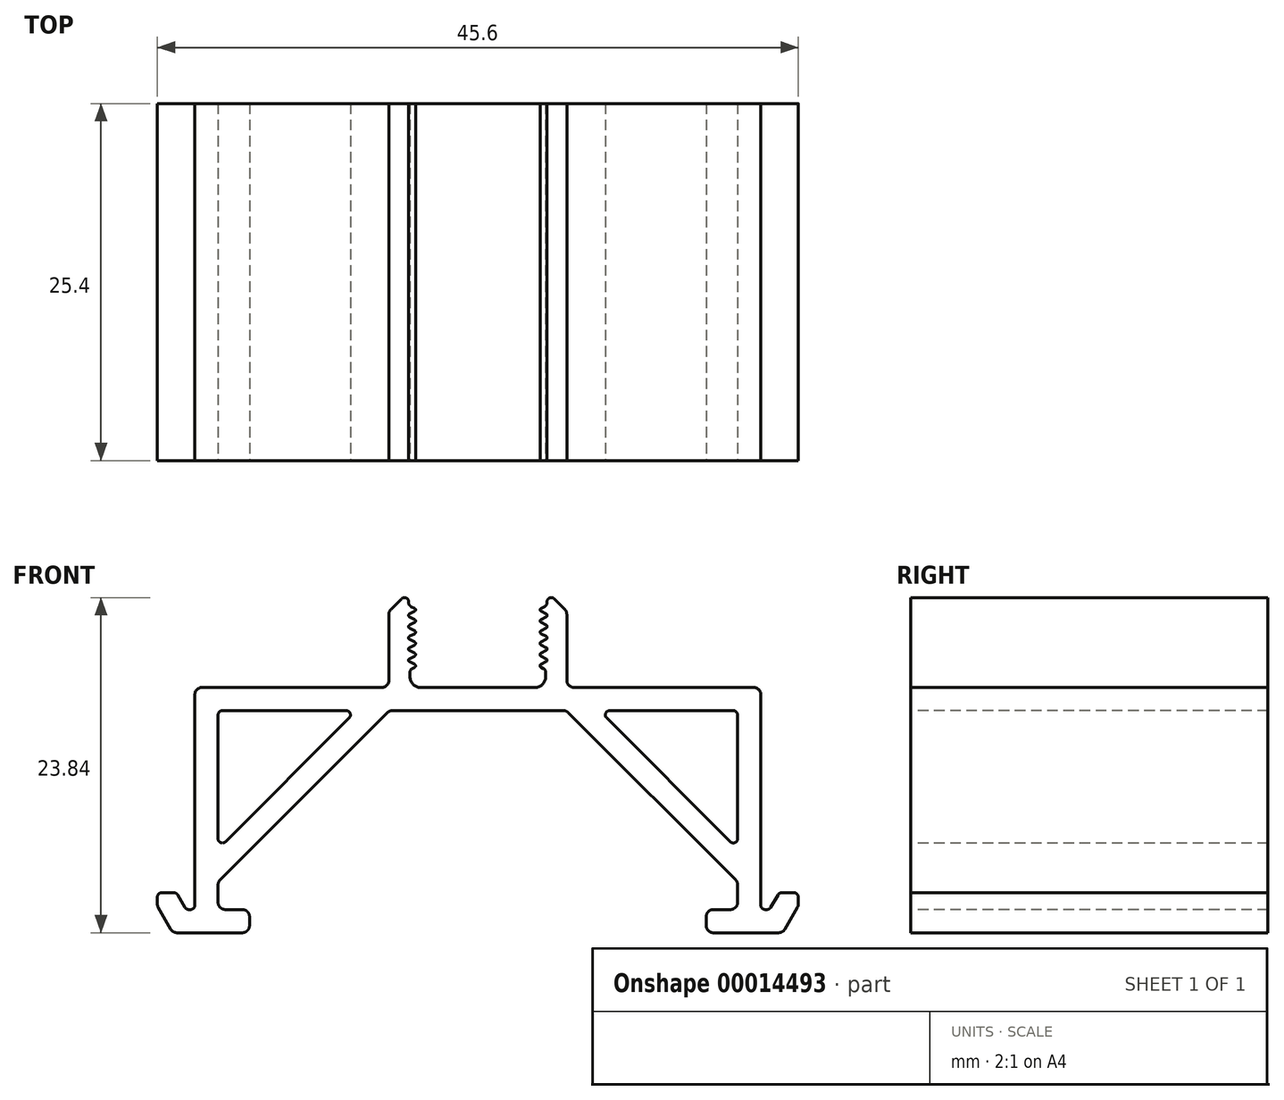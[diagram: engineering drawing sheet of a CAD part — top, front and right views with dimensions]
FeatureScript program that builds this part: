
annotation { "Feature Type Name" : "Feature", "Feature Type Description" : "" }
export const myFeature = defineFeature(function(context is Context, id is Id, definition is map)
    precondition{}
    {
        {
            var Q0;
            Q0=qCreatedBy(makeId("Front.planeOp"),FACE);
            var sketch = newSketch(context, id + "F0", { "sketchPlane" : qUnion([Q0])});
            skArc(sketch, "E0", {"start": v(18.48, 3.57) * mm, "mid": v(18.39, 3.79) * mm, "end": v(18.17, 3.88) * mm});
            skLineSegment(sketch, "E1", {"start": v(9.37, 3.88) * mm, "end": v(18.17, 3.88) * mm});
            skArc(sketch, "E2", {"start": v(9.37, 3.88) * mm, "mid": v(9.09, 3.69) * mm, "end": v(9.15, 3.36) * mm});
            skLineSegment(sketch, "E3", {"start": v(17.96, -5.45) * mm, "end": v(9.15, 3.36) * mm});
            skArc(sketch, "E4", {"start": v(17.96, -5.45) * mm, "mid": v(18.3, -5.51) * mm, "end": v(18.48, -5.23) * mm});
            skLineSegment(sketch, "E5", {"start": v(18.48, 3.57) * mm, "end": v(18.48, -5.23) * mm});
            skLineSegment(sketch, "E6", {"start": v(-18.48, -5.23) * mm, "end": v(-18.48, 3.57) * mm});
            skArc(sketch, "E7", {"start": v(-18.48, -5.23) * mm, "mid": v(-18.3, -5.51) * mm, "end": v(-17.96, -5.45) * mm});
            skLineSegment(sketch, "E8", {"start": v(-9.15, 3.36) * mm, "end": v(-17.96, -5.45) * mm});
            skArc(sketch, "E9", {"start": v(-9.15, 3.36) * mm, "mid": v(-9.09, 3.69) * mm, "end": v(-9.37, 3.88) * mm});
            skLineSegment(sketch, "E10", {"start": v(-18.17, 3.88) * mm, "end": v(-9.37, 3.88) * mm});
            skArc(sketch, "E11", {"start": v(-18.17, 3.88) * mm, "mid": v(-18.39, 3.79) * mm, "end": v(-18.48, 3.57) * mm});
            skLineSegment(sketch, "E12", {"start": v(4.86, 10.55) * mm, "end": v(4.5, 10.36) * mm});
            skArc(sketch, "E13", {"start": v(4.5, 10.36) * mm, "mid": v(4.43, 10.26) * mm, "end": v(4.5, 10.15) * mm});
            skLineSegment(sketch, "E14", {"start": v(4.5, 10.15) * mm, "end": v(4.86, 9.97) * mm});
            skArc(sketch, "E15", {"start": v(4.86, 9.75) * mm, "mid": v(4.93, 9.86) * mm, "end": v(4.86, 9.97) * mm});
            skLineSegment(sketch, "E16", {"start": v(4.86, 9.75) * mm, "end": v(4.5, 9.57) * mm});
            skArc(sketch, "E17", {"start": v(4.5, 9.57) * mm, "mid": v(4.43, 9.46) * mm, "end": v(4.5, 9.35) * mm});
            skLineSegment(sketch, "E18", {"start": v(4.5, 9.35) * mm, "end": v(4.86, 9.17) * mm});
            skArc(sketch, "E19", {"start": v(4.86, 8.95) * mm, "mid": v(4.93, 9.06) * mm, "end": v(4.86, 9.17) * mm});
            skLineSegment(sketch, "E20", {"start": v(4.86, 8.95) * mm, "end": v(4.5, 8.77) * mm});
            skArc(sketch, "E21", {"start": v(4.5, 8.77) * mm, "mid": v(4.43, 8.66) * mm, "end": v(4.5, 8.56) * mm});
            skLineSegment(sketch, "E22", {"start": v(4.5, 8.56) * mm, "end": v(4.86, 8.37) * mm});
            skArc(sketch, "E23", {"start": v(4.86, 8.16) * mm, "mid": v(4.93, 8.26) * mm, "end": v(4.86, 8.37) * mm});
            skLineSegment(sketch, "E24", {"start": v(4.86, 8.16) * mm, "end": v(4.5, 7.97) * mm});
            skArc(sketch, "E25", {"start": v(4.5, 7.97) * mm, "mid": v(4.43, 7.86) * mm, "end": v(4.5, 7.76) * mm});
            skLineSegment(sketch, "E26", {"start": v(4.5, 7.76) * mm, "end": v(4.86, 7.57) * mm});
            skArc(sketch, "E27", {"start": v(4.86, 7.36) * mm, "mid": v(4.93, 7.47) * mm, "end": v(4.86, 7.57) * mm});
            skLineSegment(sketch, "E28", {"start": v(4.86, 7.36) * mm, "end": v(4.5, 7.17) * mm});
            skArc(sketch, "E29", {"start": v(4.5, 7.17) * mm, "mid": v(4.43, 7.07) * mm, "end": v(4.5, 6.96) * mm});
            skLineSegment(sketch, "E30", {"start": v(4.5, 6.96) * mm, "end": v(4.66, 6.88) * mm});
            skArc(sketch, "E31", {"start": v(4.83, 6.6) * mm, "mid": v(4.78, 6.77) * mm, "end": v(4.66, 6.88) * mm});
            skLineSegment(sketch, "E32", {"start": v(4.83, 6.6) * mm, "end": v(4.83, 6.3) * mm});
            skArc(sketch, "E33", {"start": v(4.07, 5.53) * mm, "mid": v(4.6, 5.75) * mm, "end": v(4.83, 6.3) * mm});
            skLineSegment(sketch, "E34", {"start": v(4.07, 5.53) * mm, "end": v(-4.07, 5.53) * mm});
            skArc(sketch, "E35", {"start": v(-4.83, 6.3) * mm, "mid": v(-4.6, 5.75) * mm, "end": v(-4.07, 5.53) * mm});
            skLineSegment(sketch, "E36", {"start": v(-4.83, 6.3) * mm, "end": v(-4.83, 6.6) * mm});
            skArc(sketch, "E37", {"start": v(-4.66, 6.88) * mm, "mid": v(-4.78, 6.77) * mm, "end": v(-4.83, 6.6) * mm});
            skLineSegment(sketch, "E38", {"start": v(-4.66, 6.88) * mm, "end": v(-4.5, 6.96) * mm});
            skArc(sketch, "E39", {"start": v(-4.5, 6.96) * mm, "mid": v(-4.43, 7.07) * mm, "end": v(-4.5, 7.17) * mm});
            skLineSegment(sketch, "E40", {"start": v(-4.5, 7.17) * mm, "end": v(-4.86, 7.36) * mm});
            skArc(sketch, "E41", {"start": v(-4.86, 7.57) * mm, "mid": v(-4.93, 7.47) * mm, "end": v(-4.86, 7.36) * mm});
            skLineSegment(sketch, "E42", {"start": v(-4.86, 7.57) * mm, "end": v(-4.5, 7.76) * mm});
            skArc(sketch, "E43", {"start": v(-4.5, 7.76) * mm, "mid": v(-4.43, 7.86) * mm, "end": v(-4.5, 7.97) * mm});
            skLineSegment(sketch, "E44", {"start": v(-4.5, 7.97) * mm, "end": v(-4.86, 8.16) * mm});
            skArc(sketch, "E45", {"start": v(-4.86, 8.37) * mm, "mid": v(-4.93, 8.26) * mm, "end": v(-4.86, 8.16) * mm});
            skLineSegment(sketch, "E46", {"start": v(-4.86, 8.37) * mm, "end": v(-4.5, 8.56) * mm});
            skArc(sketch, "E47", {"start": v(-4.5, 8.56) * mm, "mid": v(-4.43, 8.66) * mm, "end": v(-4.5, 8.77) * mm});
            skLineSegment(sketch, "E48", {"start": v(-4.5, 8.77) * mm, "end": v(-4.86, 8.95) * mm});
            skArc(sketch, "E49", {"start": v(-4.86, 9.17) * mm, "mid": v(-4.93, 9.06) * mm, "end": v(-4.86, 8.95) * mm});
            skLineSegment(sketch, "E50", {"start": v(-4.86, 9.17) * mm, "end": v(-4.5, 9.35) * mm});
            skArc(sketch, "E51", {"start": v(-4.5, 9.35) * mm, "mid": v(-4.43, 9.46) * mm, "end": v(-4.5, 9.57) * mm});
            skLineSegment(sketch, "E52", {"start": v(-4.5, 9.57) * mm, "end": v(-4.86, 9.75) * mm});
            skArc(sketch, "E53", {"start": v(-4.86, 9.97) * mm, "mid": v(-4.93, 9.86) * mm, "end": v(-4.86, 9.75) * mm});
            skLineSegment(sketch, "E54", {"start": v(-4.86, 9.97) * mm, "end": v(-4.5, 10.15) * mm});
            skArc(sketch, "E55", {"start": v(-4.5, 10.15) * mm, "mid": v(-4.43, 10.26) * mm, "end": v(-4.5, 10.36) * mm});
            skLineSegment(sketch, "E56", {"start": v(-4.5, 10.36) * mm, "end": v(-4.86, 10.55) * mm});
            skArc(sketch, "E57", {"start": v(-4.86, 10.76) * mm, "mid": v(-4.93, 10.66) * mm, "end": v(-4.86, 10.55) * mm});
            skLineSegment(sketch, "E58", {"start": v(-4.86, 10.76) * mm, "end": v(-4.5, 10.95) * mm});
            skArc(sketch, "E59", {"start": v(-4.5, 10.95) * mm, "mid": v(-4.43, 11.06) * mm, "end": v(-4.5, 11.16) * mm});
            skLineSegment(sketch, "E60", {"start": v(-4.5, 11.16) * mm, "end": v(-4.76, 11.3) * mm});
            skArc(sketch, "E61", {"start": v(-4.92, 11.6) * mm, "mid": v(-4.88, 11.42) * mm, "end": v(-4.76, 11.3) * mm});
            skArc(sketch, "E62", {"start": v(-4.92, 11.6) * mm, "mid": v(-5.1, 11.9) * mm, "end": v(-5.44, 11.83) * mm});
            skLineSegment(sketch, "E63", {"start": v(-5.44, 11.83) * mm, "end": v(-6.18, 11.1) * mm});
            skArc(sketch, "E64", {"start": v(-6.18, 11.1) * mm, "mid": v(-6.29, 10.93) * mm, "end": v(-6.33, 10.74) * mm});
            skLineSegment(sketch, "E65", {"start": v(-6.33, 10.74) * mm, "end": v(-6.33, 6.04) * mm});
            skArc(sketch, "E66", {"start": v(-6.83, 5.53) * mm, "mid": v(-6.48, 5.68) * mm, "end": v(-6.33, 6.04) * mm});
            skLineSegment(sketch, "E67", {"start": v(-6.83, 5.53) * mm, "end": v(-19.62, 5.53) * mm});
            skArc(sketch, "E68", {"start": v(-19.62, 5.53) * mm, "mid": v(-19.98, 5.38) * mm, "end": v(-20.13, 5.02) * mm});
            skLineSegment(sketch, "E69", {"start": v(-20.13, 5.02) * mm, "end": v(-20.13, -9.96) * mm});
            skArc(sketch, "E70", {"start": v(-20.43, -10.27) * mm, "mid": v(-20.22, -10.18) * mm, "end": v(-20.13, -9.96) * mm});
            skLineSegment(sketch, "E71", {"start": v(-20.43, -10.27) * mm, "end": v(-20.57, -10.27) * mm});
            skArc(sketch, "E72", {"start": v(-20.83, -10.12) * mm, "mid": v(-20.72, -10.23) * mm, "end": v(-20.57, -10.27) * mm});
            skLineSegment(sketch, "E73", {"start": v(-20.83, -10.12) * mm, "end": v(-21.34, -9.23) * mm});
            skArc(sketch, "E74", {"start": v(-21.34, -9.23) * mm, "mid": v(-21.46, -9.12) * mm, "end": v(-21.6, -9.08) * mm});
            skLineSegment(sketch, "E75", {"start": v(-21.6, -9.08) * mm, "end": v(-22.5, -9.08) * mm});
            skArc(sketch, "E76", {"start": v(-22.5, -9.08) * mm, "mid": v(-22.7, -9.17) * mm, "end": v(-22.8, -9.38) * mm});
            skLineSegment(sketch, "E77", {"start": v(-22.8, -9.38) * mm, "end": v(-22.8, -9.88) * mm});
            skArc(sketch, "E78", {"start": v(-22.8, -9.88) * mm, "mid": v(-22.78, -10.01) * mm, "end": v(-22.73, -10.13) * mm});
            skLineSegment(sketch, "E79", {"start": v(-22.73, -10.13) * mm, "end": v(-21.84, -11.67) * mm});
            skArc(sketch, "E80", {"start": v(-21.84, -11.67) * mm, "mid": v(-21.66, -11.85) * mm, "end": v(-21.4, -11.92) * mm});
            skLineSegment(sketch, "E81", {"start": v(-21.4, -11.92) * mm, "end": v(-16.75, -11.92) * mm});
            skArc(sketch, "E82", {"start": v(-16.75, -11.92) * mm, "mid": v(-16.4, -11.77) * mm, "end": v(-16.24, -11.41) * mm});
            skLineSegment(sketch, "E83", {"start": v(-16.24, -11.41) * mm, "end": v(-16.24, -10.78) * mm});
            skArc(sketch, "E84", {"start": v(-16.24, -10.78) * mm, "mid": v(-16.4, -10.42) * mm, "end": v(-16.75, -10.27) * mm});
            skLineSegment(sketch, "E85", {"start": v(-16.75, -10.27) * mm, "end": v(-17.97, -10.27) * mm});
            skArc(sketch, "E86", {"start": v(-18.48, -9.76) * mm, "mid": v(-18.33, -10.12) * mm, "end": v(-17.97, -10.27) * mm});
            skLineSegment(sketch, "E87", {"start": v(-18.48, -9.76) * mm, "end": v(-18.48, -8.51) * mm});
            skArc(sketch, "E88", {"start": v(-18.33, -8.15) * mm, "mid": v(-18.44, -8.32) * mm, "end": v(-18.48, -8.51) * mm});
            skLineSegment(sketch, "E89", {"start": v(-18.33, -8.15) * mm, "end": v(-6.45, 3.73) * mm});
            skArc(sketch, "E90", {"start": v(-6.09, 3.88) * mm, "mid": v(-6.28, 3.84) * mm, "end": v(-6.45, 3.73) * mm});
            skLineSegment(sketch, "E91", {"start": v(-6.09, 3.88) * mm, "end": v(6.09, 3.88) * mm});
            skArc(sketch, "E92", {"start": v(6.45, 3.73) * mm, "mid": v(6.28, 3.84) * mm, "end": v(6.09, 3.88) * mm});
            skLineSegment(sketch, "E93", {"start": v(6.45, 3.73) * mm, "end": v(18.33, -8.15) * mm});
            skArc(sketch, "E94", {"start": v(18.48, -8.51) * mm, "mid": v(18.44, -8.32) * mm, "end": v(18.33, -8.15) * mm});
            skLineSegment(sketch, "E95", {"start": v(18.48, -8.51) * mm, "end": v(18.48, -9.76) * mm});
            skArc(sketch, "E96", {"start": v(17.97, -10.27) * mm, "mid": v(18.33, -10.12) * mm, "end": v(18.48, -9.76) * mm});
            skLineSegment(sketch, "E97", {"start": v(17.97, -10.27) * mm, "end": v(16.75, -10.27) * mm});
            skArc(sketch, "E98", {"start": v(16.75, -10.27) * mm, "mid": v(16.4, -10.42) * mm, "end": v(16.24, -10.78) * mm});
            skLineSegment(sketch, "E99", {"start": v(16.24, -10.78) * mm, "end": v(16.24, -11.41) * mm});
            skArc(sketch, "E100", {"start": v(16.24, -11.41) * mm, "mid": v(16.4, -11.77) * mm, "end": v(16.75, -11.92) * mm});
            skLineSegment(sketch, "E101", {"start": v(16.75, -11.92) * mm, "end": v(21.4, -11.92) * mm});
            skArc(sketch, "E102", {"start": v(21.4, -11.92) * mm, "mid": v(21.66, -11.85) * mm, "end": v(21.84, -11.67) * mm});
            skLineSegment(sketch, "E103", {"start": v(21.84, -11.67) * mm, "end": v(22.73, -10.13) * mm});
            skArc(sketch, "E104", {"start": v(22.73, -10.13) * mm, "mid": v(22.78, -10.01) * mm, "end": v(22.8, -9.88) * mm});
            skLineSegment(sketch, "E105", {"start": v(22.8, -9.88) * mm, "end": v(22.8, -9.38) * mm});
            skArc(sketch, "E106", {"start": v(22.8, -9.38) * mm, "mid": v(22.7, -9.17) * mm, "end": v(22.5, -9.08) * mm});
            skLineSegment(sketch, "E107", {"start": v(22.5, -9.08) * mm, "end": v(21.6, -9.08) * mm});
            skArc(sketch, "E108", {"start": v(21.6, -9.08) * mm, "mid": v(21.46, -9.12) * mm, "end": v(21.34, -9.23) * mm});
            skLineSegment(sketch, "E109", {"start": v(21.34, -9.23) * mm, "end": v(20.83, -10.12) * mm});
            skArc(sketch, "E110", {"start": v(20.57, -10.27) * mm, "mid": v(20.72, -10.23) * mm, "end": v(20.83, -10.12) * mm});
            skLineSegment(sketch, "E111", {"start": v(20.57, -10.27) * mm, "end": v(20.43, -10.27) * mm});
            skArc(sketch, "E112", {"start": v(20.13, -9.96) * mm, "mid": v(20.22, -10.18) * mm, "end": v(20.43, -10.27) * mm});
            skLineSegment(sketch, "E113", {"start": v(20.13, -9.96) * mm, "end": v(20.13, 5.02) * mm});
            skArc(sketch, "E114", {"start": v(20.13, 5.02) * mm, "mid": v(19.98, 5.38) * mm, "end": v(19.62, 5.53) * mm});
            skLineSegment(sketch, "E115", {"start": v(19.62, 5.53) * mm, "end": v(6.83, 5.53) * mm});
            skArc(sketch, "E116", {"start": v(6.33, 6.04) * mm, "mid": v(6.48, 5.68) * mm, "end": v(6.83, 5.53) * mm});
            skLineSegment(sketch, "E117", {"start": v(6.33, 6.04) * mm, "end": v(6.33, 10.74) * mm});
            skArc(sketch, "E118", {"start": v(6.33, 10.74) * mm, "mid": v(6.29, 10.93) * mm, "end": v(6.18, 11.1) * mm});
            skLineSegment(sketch, "E119", {"start": v(6.18, 11.1) * mm, "end": v(5.44, 11.83) * mm});
            skArc(sketch, "E120", {"start": v(5.44, 11.83) * mm, "mid": v(5.1, 11.9) * mm, "end": v(4.92, 11.6) * mm});
            skArc(sketch, "E121", {"start": v(4.76, 11.3) * mm, "mid": v(4.88, 11.42) * mm, "end": v(4.92, 11.6) * mm});
            skLineSegment(sketch, "E122", {"start": v(4.76, 11.3) * mm, "end": v(4.5, 11.16) * mm});
            skArc(sketch, "E123", {"start": v(4.5, 11.16) * mm, "mid": v(4.43, 11.06) * mm, "end": v(4.5, 10.95) * mm});
            skLineSegment(sketch, "E124", {"start": v(4.5, 10.95) * mm, "end": v(4.86, 10.76) * mm});
            skArc(sketch, "E125", {"start": v(4.86, 10.55) * mm, "mid": v(4.93, 10.66) * mm, "end": v(4.86, 10.76) * mm});
            skSolve(sketch);
        }
        {
            var Q0;
            Q0=makeQuery(id+"F0.imprint","IMPRINT",FACE,{"disambiguationData":[TD([[makeQuery(id+"F0.imprint","IMPRINT",EDGE,{"derivedFrom":sQuery(id+"F0.wireOp",EDGE,"E0")}),1.0]])]});
            var Q1;
            Q1=makeQuery(id+"F0.imprint","IMPRINT",FACE,{"disambiguationData":[TD([[makeQuery(id+"F0.imprint","IMPRINT",EDGE,{"derivedFrom":sQuery(id+"F0.wireOp",EDGE,"E6")}),-1.0]])]});
            var Q2;
            Q2=sQuery(id+"F0.wireOp",EDGE,"E67");
            var Q3;
            Q3=sQuery(id+"F0.wireOp",EDGE,"E115");
            var Q4;
            Q4=sQuery(id+"F0.wireOp",EDGE,"E91");
            var Q5;
            Q5=sQuery(id+"F0.wireOp",EDGE,"E93");
            var Q6;
            Q6=sQuery(id+"F0.wireOp",EDGE,"E69");
            var Q7;
            Q7=sQuery(id+"F0.wireOp",EDGE,"E117");
            var Q8;
            Q8=sQuery(id+"F0.wireOp",EDGE,"E101");
            var Q9;
            Q9=sQuery(id+"F0.wireOp",EDGE,"E79");
            var Q10;
            Q10=sQuery(id+"F0.wireOp",EDGE,"E1");
            var Q11;
            Q11=sQuery(id+"F0.wireOp",EDGE,"E3");
            var Q12;
            Q12=sQuery(id+"F0.wireOp",EDGE,"E5");
            var Q13;
            Q13=sQuery(id+"F0.wireOp",EDGE,"E6");
            var Q14;
            Q14=sQuery(id+"F0.wireOp",EDGE,"E8");
            var Q15;
            Q15=sQuery(id+"F0.wireOp",EDGE,"E10");
            var Q16;
            Q16=sQuery(id+"F0.wireOp",EDGE,"E81");
            var Q17;
            Q17=sQuery(id+"F0.wireOp",EDGE,"E65");
            var Q18;
            Q18=sQuery(id+"F0.wireOp",EDGE,"E113");
            var Q19;
            Q19=sQuery(id+"F0.wireOp",EDGE,"E89");
            var Q20;
            Q20=sQuery(id+"F0.wireOp",EDGE,"E34");
            var Q21;
            Q21=sQuery(id+"F0.wireOp",EDGE,"E106");
            var Q22;
            Q22=sQuery(id+"F0.wireOp",EDGE,"E90");
            var Q23;
            Q23=sQuery(id+"F0.wireOp",EDGE,"E74");
            var Q24;
            Q24=sQuery(id+"F0.wireOp",EDGE,"E83");
            var Q25;
            Q25=sQuery(id+"F0.wireOp",EDGE,"E35");
            var Q26;
            Q26=sQuery(id+"F0.wireOp",EDGE,"E99");
            var Q27;
            Q27=sQuery(id+"F0.wireOp",EDGE,"E107");
            var Q28;
            Q28=sQuery(id+"F0.wireOp",EDGE,"E75");
            var Q29;
            Q29=sQuery(id+"F0.wireOp",EDGE,"E84");
            var Q30;
            Q30=sQuery(id+"F0.wireOp",EDGE,"E68");
            var Q31;
            Q31=sQuery(id+"F0.wireOp",EDGE,"E116");
            var Q32;
            Q32=sQuery(id+"F0.wireOp",EDGE,"E100");
            var Q33;
            Q33=sQuery(id+"F0.wireOp",EDGE,"E108");
            var Q34;
            Q34=sQuery(id+"F0.wireOp",EDGE,"E92");
            var Q35;
            Q35=sQuery(id+"F0.wireOp",EDGE,"E76");
            var Q36;
            Q36=sQuery(id+"F0.wireOp",EDGE,"E85");
            var Q37;
            Q37=sQuery(id+"F0.wireOp",EDGE,"E94");
            var Q38;
            Q38=sQuery(id+"F0.wireOp",EDGE,"E86");
            var Q39;
            Q39=sQuery(id+"F0.wireOp",EDGE,"E63");
            var Q40;
            Q40=sQuery(id+"F0.wireOp",EDGE,"E118");
            var Q41;
            Q41=sQuery(id+"F0.wireOp",EDGE,"E95");
            var Q42;
            Q42=sQuery(id+"F0.wireOp",EDGE,"E102");
            var Q43;
            Q43=sQuery(id+"F0.wireOp",EDGE,"E0");
            var Q44;
            Q44=sQuery(id+"F0.wireOp",EDGE,"E7");
            var Q45;
            Q45=sQuery(id+"F0.wireOp",EDGE,"E9");
            var Q46;
            Q46=sQuery(id+"F0.wireOp",EDGE,"E11");
            var Q47;
            Q47=sQuery(id+"F0.wireOp",EDGE,"E96");
            var Q48;
            Q48=sQuery(id+"F0.wireOp",EDGE,"E119");
            var Q49;
            Q49=sQuery(id+"F0.wireOp",EDGE,"E103");
            var Q50;
            Q50=sQuery(id+"F0.wireOp",EDGE,"E87");
            var Q51;
            Q51=sQuery(id+"F0.wireOp",EDGE,"E64");
            var Q52;
            Q52=sQuery(id+"F0.wireOp",EDGE,"E88");
            var Q53;
            Q53=sQuery(id+"F0.wireOp",EDGE,"E33");
            var Q54;
            Q54=sQuery(id+"F0.wireOp",EDGE,"E97");
            var Q55;
            Q55=sQuery(id+"F0.wireOp",EDGE,"E105");
            var Q56;
            Q56=sQuery(id+"F0.wireOp",EDGE,"E73");
            var Q57;
            Q57=sQuery(id+"F0.wireOp",EDGE,"E82");
            var Q58;
            Q58=sQuery(id+"F0.wireOp",EDGE,"E66");
            var Q59;
            Q59=sQuery(id+"F0.wireOp",EDGE,"E114");
            var Q60;
            Q60=sQuery(id+"F0.wireOp",EDGE,"E98");
            var Q61;
            Q61=sQuery(id+"F0.wireOp",EDGE,"E109");
            var Q62;
            Q62=sQuery(id+"F0.wireOp",EDGE,"E62");
            var Q63;
            Q63=sQuery(id+"F0.wireOp",EDGE,"E70");
            var Q64;
            Q64=sQuery(id+"F0.wireOp",EDGE,"E2");
            var Q65;
            Q65=sQuery(id+"F0.wireOp",EDGE,"E4");
            var Q66;
            Q66=sQuery(id+"F0.wireOp",EDGE,"E80");
            var Q67;
            Q67=sQuery(id+"F0.wireOp",EDGE,"E120");
            var Q68;
            Q68=sQuery(id+"F0.wireOp",EDGE,"E104");
            var Q69;
            Q69=sQuery(id+"F0.wireOp",EDGE,"E72");
            var Q70;
            Q70=sQuery(id+"F0.wireOp",EDGE,"E77");
            var Q71;
            Q71=sQuery(id+"F0.wireOp",EDGE,"E78");
            var Q72;
            Q72=sQuery(id+"F0.wireOp",EDGE,"E71");
            var Q73;
            Q73=sQuery(id+"F0.wireOp",EDGE,"E59");
            var Q74;
            Q74=sQuery(id+"F0.wireOp",EDGE,"E61");
            var Q75;
            Q75=sQuery(id+"F0.wireOp",EDGE,"E36");
            var Q76;
            Q76=sQuery(id+"F0.wireOp",EDGE,"E60");
            var Q77;
            Q77=sQuery(id+"F0.wireOp",EDGE,"E124");
            var Q78;
            Q78=sQuery(id+"F0.wireOp",EDGE,"E37");
            var Q79;
            Q79=sQuery(id+"F0.wireOp",EDGE,"E57");
            var Q80;
            Q80=sQuery(id+"F0.wireOp",EDGE,"E121");
            var Q81;
            Q81=sQuery(id+"F0.wireOp",EDGE,"E58");
            var Q82;
            Q82=sQuery(id+"F0.wireOp",EDGE,"E122");
            var Q83;
            Q83=sQuery(id+"F0.wireOp",EDGE,"E43");
            var Q84;
            Q84=sQuery(id+"F0.wireOp",EDGE,"E123");
            var Q85;
            Q85=sQuery(id+"F0.wireOp",EDGE,"E125");
            var Q86;
            Q86=sQuery(id+"F0.wireOp",EDGE,"E31");
            var Q87;
            Q87=sQuery(id+"F0.wireOp",EDGE,"E111");
            var Q88;
            Q88=sQuery(id+"F0.wireOp",EDGE,"E12");
            var Q89;
            Q89=sQuery(id+"F0.wireOp",EDGE,"E112");
            var Q90;
            Q90=sQuery(id+"F0.wireOp",EDGE,"E39");
            var Q91;
            Q91=sQuery(id+"F0.wireOp",EDGE,"E32");
            var Q92;
            Q92=sQuery(id+"F0.wireOp",EDGE,"E40");
            var Q93;
            Q93=sQuery(id+"F0.wireOp",EDGE,"E41");
            var Q94;
            Q94=sQuery(id+"F0.wireOp",EDGE,"E42");
            var Q95;
            Q95=sQuery(id+"F0.wireOp",EDGE,"E52");
            var Q96;
            Q96=sQuery(id+"F0.wireOp",EDGE,"E44");
            var Q97;
            Q97=sQuery(id+"F0.wireOp",EDGE,"E28");
            var Q98;
            Q98=sQuery(id+"F0.wireOp",EDGE,"E53");
            var Q99;
            Q99=sQuery(id+"F0.wireOp",EDGE,"E46");
            var Q100;
            Q100=sQuery(id+"F0.wireOp",EDGE,"E30");
            var Q101;
            Q101=sQuery(id+"F0.wireOp",EDGE,"E110");
            var Q102;
            Q102=sQuery(id+"F0.wireOp",EDGE,"E22");
            var Q103;
            Q103=sQuery(id+"F0.wireOp",EDGE,"E54");
            var Q104;
            Q104=sQuery(id+"F0.wireOp",EDGE,"E47");
            var Q105;
            Q105=sQuery(id+"F0.wireOp",EDGE,"E38");
            var Q106;
            Q106=sQuery(id+"F0.wireOp",EDGE,"E14");
            var Q107;
            Q107=sQuery(id+"F0.wireOp",EDGE,"E48");
            var Q108;
            Q108=sQuery(id+"F0.wireOp",EDGE,"E56");
            var Q109;
            Q109=sQuery(id+"F0.wireOp",EDGE,"E24");
            var Q110;
            Q110=sQuery(id+"F0.wireOp",EDGE,"E25");
            var Q111;
            Q111=sQuery(id+"F0.wireOp",EDGE,"E50");
            var Q112;
            Q112=sQuery(id+"F0.wireOp",EDGE,"E26");
            var Q113;
            Q113=sQuery(id+"F0.wireOp",EDGE,"E51");
            var Q114;
            Q114=sQuery(id+"F0.wireOp",EDGE,"E27");
            var Q115;
            Q115=sQuery(id+"F0.wireOp",EDGE,"E20");
            var Q116;
            Q116=sQuery(id+"F0.wireOp",EDGE,"E45");
            var Q117;
            Q117=sQuery(id+"F0.wireOp",EDGE,"E29");
            var Q118;
            Q118=sQuery(id+"F0.wireOp",EDGE,"E21");
            var Q119;
            Q119=sQuery(id+"F0.wireOp",EDGE,"E13");
            var Q120;
            Q120=sQuery(id+"F0.wireOp",EDGE,"E15");
            var Q121;
            Q121=sQuery(id+"F0.wireOp",EDGE,"E55");
            var Q122;
            Q122=sQuery(id+"F0.wireOp",EDGE,"E23");
            var Q123;
            Q123=sQuery(id+"F0.wireOp",EDGE,"E16");
            var Q124;
            Q124=sQuery(id+"F0.wireOp",EDGE,"E17");
            var Q125;
            Q125=sQuery(id+"F0.wireOp",EDGE,"E49");
            var Q126;
            Q126=sQuery(id+"F0.wireOp",EDGE,"E18");
            var Q127;
            Q127=sQuery(id+"F0.wireOp",EDGE,"E19");
            extrude(context, id + "F1", {"entities" : qUnion([Q0, Q1]), "bodyType" : ToolBodyType.SURFACE, "surfaceEntities" : qUnion([Q2, Q3, Q4, Q5, Q6, Q7, Q8, Q9, Q10, Q11, Q12, Q13, Q14, Q15, Q16, Q17, Q18, Q19, Q20, Q21, Q22, Q23, Q24, Q25, Q26, Q27, Q28, Q29, Q30, Q31, Q32, Q33, Q34, Q35, Q36, Q37, Q38, Q39, Q40, Q41, Q42, Q43, Q44, Q45, Q46, Q47, Q48, Q49, Q50, Q51, Q52, Q53, Q54, Q55, Q56, Q57, Q58, Q59, Q60, Q61, Q62, Q63, Q64, Q65, Q66, Q67, Q68, Q69, Q70, Q71, Q72, Q73, Q74, Q75, Q76, Q77, Q78, Q79, Q80, Q81, Q82, Q83, Q84, Q85, Q86, Q87, Q88, Q89, Q90, Q91, Q92, Q93, Q94, Q95, Q96, Q97, Q98, Q99, Q100, Q101, Q102, Q103, Q104, Q105, Q106, Q107, Q108, Q109, Q110, Q111, Q112, Q113, Q114, Q115, Q116, Q117, Q118, Q119, Q120, Q121, Q122, Q123, Q124, Q125, Q126, Q127]), "depth" : 25.4 * mm});
        }
    });
